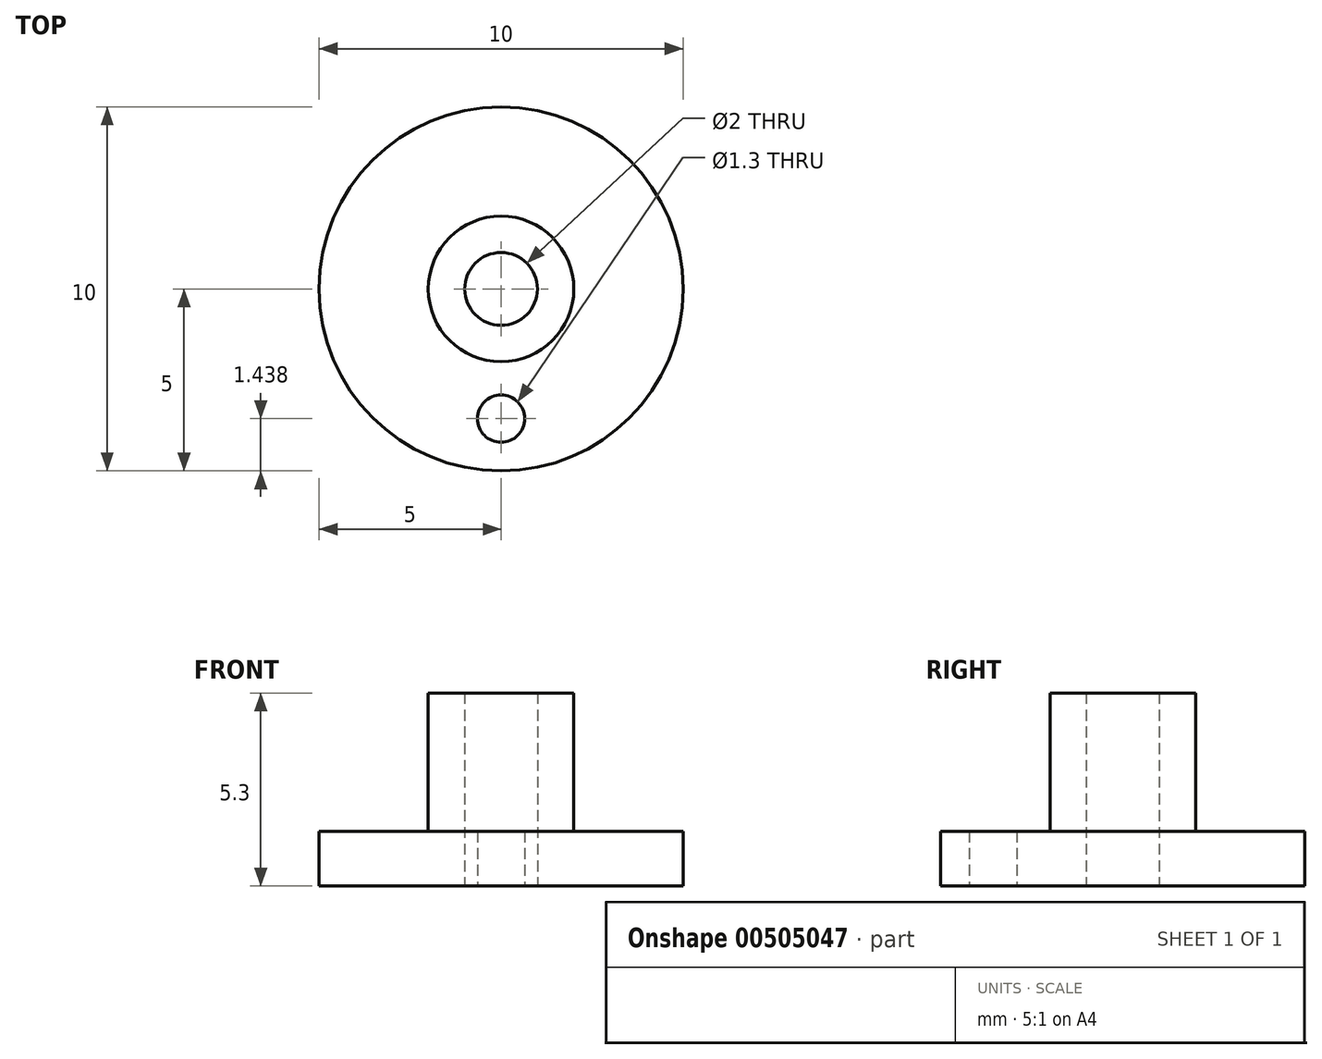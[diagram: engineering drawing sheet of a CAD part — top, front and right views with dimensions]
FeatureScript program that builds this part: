
annotation { "Feature Type Name" : "Feature", "Feature Type Description" : "" }
export const myFeature = defineFeature(function(context is Context, id is Id, definition is map)
    precondition{}
    {
        {
            var Q0;
            Q0=qCreatedBy(makeId("Top.planeOp"),FACE);
            var sketch = newSketch(context, id + "F0", { "sketchPlane" : qUnion([Q0])});
            skCircle(sketch, "E0", {"center": v(0, 0) * mm, "radius": 5 * mm});
            skCircle(sketch, "E1", {"center": v(0, 0) * mm, "radius": 1 * mm});
            skSolve(sketch);
        }
        {
            var Q0;
            Q0=makeQuery(id+"F0.imprint","IMPRINT",FACE,{"disambiguationData":[TD([[makeQuery(id+"F0.imprint","IMPRINT",EDGE,{"derivedFrom":sQuery(id+"F0.wireOp",EDGE,"E1")}),-1.0]])]});
            var Q1;
            {var subQ0=sQuery(id+"F0.wireOp",EDGE,"EI4zZE9N-whVI-OPHs-3LS9-Eucb53RtoGpZ");var subQ1=sQuery(id+"F0.wireOp",EDGE,"E0");var subQ2=makeQuery(id+"F0.imprint","INTERSECT",VERTEX,{"derivedFrom":[subQ1,subQ0]});Q1=makeQuery(id+"F0.imprint","IMPRINT",FACE,{"disambiguationData":[TD([[makeQuery(id+"F0.imprint","IMPRINT",EDGE,{"disambiguationData":[TD([[subQ2,1.0]])],"derivedFrom":subQ1}),-1.0]])]});}
            var Q2;
            {var subQ0=sQuery(id+"F0.wireOp",EDGE,"6d7b41f3-6400-49b5-a72e-f197a9a28993.24.0");var subQ1=sQuery(id+"F0.wireOp",EDGE,"E0");var subQ2=makeQuery(id+"F0.imprint","INTERSECT",VERTEX,{"derivedFrom":[subQ1,subQ0]});Q2=makeQuery(id+"F0.imprint","IMPRINT",FACE,{"disambiguationData":[TD([[makeQuery(id+"F0.imprint","IMPRINT",EDGE,{"disambiguationData":[TD([[subQ2,1.0]])],"derivedFrom":subQ1}),-1.0]])]});}
            var Q3;
            {var subQ0=sQuery(id+"F0.wireOp",EDGE,"6d7b41f3-6400-49b5-a72e-f197a9a28993.25.0");var subQ1=sQuery(id+"F0.wireOp",EDGE,"E0");var subQ2=makeQuery(id+"F0.imprint","INTERSECT",VERTEX,{"derivedFrom":[subQ1,subQ0]});Q3=makeQuery(id+"F0.imprint","IMPRINT",FACE,{"disambiguationData":[TD([[makeQuery(id+"F0.imprint","IMPRINT",EDGE,{"disambiguationData":[TD([[subQ2,1.0]])],"derivedFrom":subQ1}),-1.0]])]});}
            var Q4;
            {var subQ0=sQuery(id+"F0.wireOp",EDGE,"6d7b41f3-6400-49b5-a72e-f197a9a28993.26.0");var subQ1=sQuery(id+"F0.wireOp",EDGE,"E0");var subQ2=makeQuery(id+"F0.imprint","INTERSECT",VERTEX,{"derivedFrom":[subQ1,subQ0]});Q4=makeQuery(id+"F0.imprint","IMPRINT",FACE,{"disambiguationData":[TD([[makeQuery(id+"F0.imprint","IMPRINT",EDGE,{"disambiguationData":[TD([[subQ2,1.0]])],"derivedFrom":subQ1}),-1.0]])]});}
            var Q5;
            {var subQ0=sQuery(id+"F0.wireOp",EDGE,"6d7b41f3-6400-49b5-a72e-f197a9a28993.27.0");var subQ1=sQuery(id+"F0.wireOp",EDGE,"E0");var subQ2=makeQuery(id+"F0.imprint","INTERSECT",VERTEX,{"derivedFrom":[subQ1,subQ0]});Q5=makeQuery(id+"F0.imprint","IMPRINT",FACE,{"disambiguationData":[TD([[makeQuery(id+"F0.imprint","IMPRINT",EDGE,{"disambiguationData":[TD([[subQ2,1.0]])],"derivedFrom":subQ1}),-1.0]])]});}
            var Q6;
            {var subQ0=sQuery(id+"F0.wireOp",EDGE,"6d7b41f3-6400-49b5-a72e-f197a9a28993.28.0");var subQ1=sQuery(id+"F0.wireOp",EDGE,"E0");var subQ2=makeQuery(id+"F0.imprint","INTERSECT",VERTEX,{"derivedFrom":[subQ1,subQ0]});Q6=makeQuery(id+"F0.imprint","IMPRINT",FACE,{"disambiguationData":[TD([[makeQuery(id+"F0.imprint","IMPRINT",EDGE,{"disambiguationData":[TD([[subQ2,1.0]])],"derivedFrom":subQ1}),-1.0]])]});}
            var Q7;
            {var subQ0=sQuery(id+"F0.wireOp",EDGE,"6d7b41f3-6400-49b5-a72e-f197a9a28993.29.0");var subQ1=sQuery(id+"F0.wireOp",EDGE,"E0");var subQ2=makeQuery(id+"F0.imprint","INTERSECT",VERTEX,{"derivedFrom":[subQ1,subQ0]});Q7=makeQuery(id+"F0.imprint","IMPRINT",FACE,{"disambiguationData":[TD([[makeQuery(id+"F0.imprint","IMPRINT",EDGE,{"disambiguationData":[TD([[subQ2,1.0]])],"derivedFrom":subQ1}),-1.0]])]});}
            var Q8;
            {var subQ0=sQuery(id+"F0.wireOp",EDGE,"6d7b41f3-6400-49b5-a72e-f197a9a28993.30.0");var subQ1=sQuery(id+"F0.wireOp",EDGE,"E0");var subQ2=makeQuery(id+"F0.imprint","INTERSECT",VERTEX,{"derivedFrom":[subQ1,subQ0]});Q8=makeQuery(id+"F0.imprint","IMPRINT",FACE,{"disambiguationData":[TD([[makeQuery(id+"F0.imprint","IMPRINT",EDGE,{"disambiguationData":[TD([[subQ2,1.0]])],"derivedFrom":subQ1}),-1.0]])]});}
            var Q9;
            {var subQ0=sQuery(id+"F0.wireOp",EDGE,"rxgSa6x3-vu4U-r9f0-bHfC-lMe1TVJ3Zobz");var subQ1=sQuery(id+"F0.wireOp",EDGE,"E0");var subQ2=makeQuery(id+"F0.imprint","INTERSECT",VERTEX,{"derivedFrom":[subQ1,subQ0]});Q9=makeQuery(id+"F0.imprint","IMPRINT",FACE,{"disambiguationData":[TD([[makeQuery(id+"F0.imprint","IMPRINT",EDGE,{"disambiguationData":[TD([[subQ2,-1.0]])],"derivedFrom":subQ1}),-1.0]])]});}
            var Q10;
            {var subQ0=sQuery(id+"F0.wireOp",EDGE,"6d7b41f3-6400-49b5-a72e-f197a9a28993.1.0");var subQ1=sQuery(id+"F0.wireOp",EDGE,"E0");var subQ2=makeQuery(id+"F0.imprint","INTERSECT",VERTEX,{"derivedFrom":[subQ1,subQ0]});Q10=makeQuery(id+"F0.imprint","IMPRINT",FACE,{"disambiguationData":[TD([[makeQuery(id+"F0.imprint","IMPRINT",EDGE,{"disambiguationData":[TD([[subQ2,1.0]])],"derivedFrom":subQ1}),-1.0]])]});}
            var Q11;
            {var subQ0=sQuery(id+"F0.wireOp",EDGE,"6d7b41f3-6400-49b5-a72e-f197a9a28993.2.0");var subQ1=sQuery(id+"F0.wireOp",EDGE,"E0");var subQ2=makeQuery(id+"F0.imprint","INTERSECT",VERTEX,{"derivedFrom":[subQ1,subQ0]});Q11=makeQuery(id+"F0.imprint","IMPRINT",FACE,{"disambiguationData":[TD([[makeQuery(id+"F0.imprint","IMPRINT",EDGE,{"disambiguationData":[TD([[subQ2,1.0]])],"derivedFrom":subQ1}),-1.0]])]});}
            var Q12;
            {var subQ0=sQuery(id+"F0.wireOp",EDGE,"6d7b41f3-6400-49b5-a72e-f197a9a28993.3.0");var subQ1=sQuery(id+"F0.wireOp",EDGE,"E0");var subQ2=makeQuery(id+"F0.imprint","INTERSECT",VERTEX,{"derivedFrom":[subQ1,subQ0]});Q12=makeQuery(id+"F0.imprint","IMPRINT",FACE,{"disambiguationData":[TD([[makeQuery(id+"F0.imprint","IMPRINT",EDGE,{"disambiguationData":[TD([[subQ2,1.0]])],"derivedFrom":subQ1}),-1.0]])]});}
            var Q13;
            {var subQ0=sQuery(id+"F0.wireOp",EDGE,"6d7b41f3-6400-49b5-a72e-f197a9a28993.4.0");var subQ1=sQuery(id+"F0.wireOp",EDGE,"E0");var subQ2=makeQuery(id+"F0.imprint","INTERSECT",VERTEX,{"derivedFrom":[subQ1,subQ0]});Q13=makeQuery(id+"F0.imprint","IMPRINT",FACE,{"disambiguationData":[TD([[makeQuery(id+"F0.imprint","IMPRINT",EDGE,{"disambiguationData":[TD([[subQ2,1.0]])],"derivedFrom":subQ1}),-1.0]])]});}
            var Q14;
            {var subQ0=sQuery(id+"F0.wireOp",EDGE,"6d7b41f3-6400-49b5-a72e-f197a9a28993.5.0");var subQ1=sQuery(id+"F0.wireOp",EDGE,"E0");var subQ2=makeQuery(id+"F0.imprint","INTERSECT",VERTEX,{"derivedFrom":[subQ1,subQ0]});Q14=makeQuery(id+"F0.imprint","IMPRINT",FACE,{"disambiguationData":[TD([[makeQuery(id+"F0.imprint","IMPRINT",EDGE,{"disambiguationData":[TD([[subQ2,1.0]])],"derivedFrom":subQ1}),-1.0]])]});}
            var Q15;
            {var subQ0=sQuery(id+"F0.wireOp",EDGE,"6d7b41f3-6400-49b5-a72e-f197a9a28993.6.0");var subQ1=sQuery(id+"F0.wireOp",EDGE,"E0");var subQ2=makeQuery(id+"F0.imprint","INTERSECT",VERTEX,{"derivedFrom":[subQ1,subQ0]});Q15=makeQuery(id+"F0.imprint","IMPRINT",FACE,{"disambiguationData":[TD([[makeQuery(id+"F0.imprint","IMPRINT",EDGE,{"disambiguationData":[TD([[subQ2,1.0]])],"derivedFrom":subQ1}),-1.0]])]});}
            var Q16;
            {var subQ0=sQuery(id+"F0.wireOp",EDGE,"6d7b41f3-6400-49b5-a72e-f197a9a28993.7.0");var subQ1=sQuery(id+"F0.wireOp",EDGE,"E0");var subQ2=makeQuery(id+"F0.imprint","INTERSECT",VERTEX,{"derivedFrom":[subQ1,subQ0]});Q16=makeQuery(id+"F0.imprint","IMPRINT",FACE,{"disambiguationData":[TD([[makeQuery(id+"F0.imprint","IMPRINT",EDGE,{"disambiguationData":[TD([[subQ2,1.0]])],"derivedFrom":subQ1}),-1.0]])]});}
            var Q17;
            {var subQ0=sQuery(id+"F0.wireOp",EDGE,"6d7b41f3-6400-49b5-a72e-f197a9a28993.8.0");var subQ1=sQuery(id+"F0.wireOp",EDGE,"E0");var subQ2=makeQuery(id+"F0.imprint","INTERSECT",VERTEX,{"derivedFrom":[subQ1,subQ0]});Q17=makeQuery(id+"F0.imprint","IMPRINT",FACE,{"disambiguationData":[TD([[makeQuery(id+"F0.imprint","IMPRINT",EDGE,{"disambiguationData":[TD([[subQ2,1.0]])],"derivedFrom":subQ1}),-1.0]])]});}
            var Q18;
            {var subQ0=sQuery(id+"F0.wireOp",EDGE,"6d7b41f3-6400-49b5-a72e-f197a9a28993.9.0");var subQ1=sQuery(id+"F0.wireOp",EDGE,"E0");var subQ2=makeQuery(id+"F0.imprint","INTERSECT",VERTEX,{"derivedFrom":[subQ1,subQ0]});Q18=makeQuery(id+"F0.imprint","IMPRINT",FACE,{"disambiguationData":[TD([[makeQuery(id+"F0.imprint","IMPRINT",EDGE,{"disambiguationData":[TD([[subQ2,1.0]])],"derivedFrom":subQ1}),-1.0]])]});}
            var Q19;
            {var subQ0=sQuery(id+"F0.wireOp",EDGE,"6d7b41f3-6400-49b5-a72e-f197a9a28993.10.0");var subQ1=sQuery(id+"F0.wireOp",EDGE,"E0");var subQ2=makeQuery(id+"F0.imprint","INTERSECT",VERTEX,{"derivedFrom":[subQ1,subQ0]});Q19=makeQuery(id+"F0.imprint","IMPRINT",FACE,{"disambiguationData":[TD([[makeQuery(id+"F0.imprint","IMPRINT",EDGE,{"disambiguationData":[TD([[subQ2,1.0]])],"derivedFrom":subQ1}),-1.0]])]});}
            var Q20;
            {var subQ0=sQuery(id+"F0.wireOp",EDGE,"6d7b41f3-6400-49b5-a72e-f197a9a28993.11.0");var subQ1=sQuery(id+"F0.wireOp",EDGE,"E0");var subQ2=makeQuery(id+"F0.imprint","INTERSECT",VERTEX,{"derivedFrom":[subQ1,subQ0]});Q20=makeQuery(id+"F0.imprint","IMPRINT",FACE,{"disambiguationData":[TD([[makeQuery(id+"F0.imprint","IMPRINT",EDGE,{"disambiguationData":[TD([[subQ2,1.0]])],"derivedFrom":subQ1}),-1.0]])]});}
            var Q21;
            {var subQ0=sQuery(id+"F0.wireOp",EDGE,"6d7b41f3-6400-49b5-a72e-f197a9a28993.12.0");var subQ1=sQuery(id+"F0.wireOp",EDGE,"E0");var subQ2=makeQuery(id+"F0.imprint","INTERSECT",VERTEX,{"derivedFrom":[subQ1,subQ0]});Q21=makeQuery(id+"F0.imprint","IMPRINT",FACE,{"disambiguationData":[TD([[makeQuery(id+"F0.imprint","IMPRINT",EDGE,{"disambiguationData":[TD([[subQ2,1.0]])],"derivedFrom":subQ1}),-1.0]])]});}
            var Q22;
            {var subQ0=sQuery(id+"F0.wireOp",EDGE,"6d7b41f3-6400-49b5-a72e-f197a9a28993.13.0");var subQ1=sQuery(id+"F0.wireOp",EDGE,"E0");var subQ2=makeQuery(id+"F0.imprint","INTERSECT",VERTEX,{"derivedFrom":[subQ1,subQ0]});Q22=makeQuery(id+"F0.imprint","IMPRINT",FACE,{"disambiguationData":[TD([[makeQuery(id+"F0.imprint","IMPRINT",EDGE,{"disambiguationData":[TD([[subQ2,1.0]])],"derivedFrom":subQ1}),-1.0]])]});}
            var Q23;
            {var subQ0=sQuery(id+"F0.wireOp",EDGE,"6d7b41f3-6400-49b5-a72e-f197a9a28993.14.0");var subQ1=sQuery(id+"F0.wireOp",EDGE,"E0");var subQ2=makeQuery(id+"F0.imprint","INTERSECT",VERTEX,{"derivedFrom":[subQ1,subQ0]});Q23=makeQuery(id+"F0.imprint","IMPRINT",FACE,{"disambiguationData":[TD([[makeQuery(id+"F0.imprint","IMPRINT",EDGE,{"disambiguationData":[TD([[subQ2,1.0]])],"derivedFrom":subQ1}),-1.0]])]});}
            var Q24;
            {var subQ0=sQuery(id+"F0.wireOp",EDGE,"6d7b41f3-6400-49b5-a72e-f197a9a28993.15.0");var subQ1=sQuery(id+"F0.wireOp",EDGE,"E0");var subQ2=makeQuery(id+"F0.imprint","INTERSECT",VERTEX,{"derivedFrom":[subQ1,subQ0]});Q24=makeQuery(id+"F0.imprint","IMPRINT",FACE,{"disambiguationData":[TD([[makeQuery(id+"F0.imprint","IMPRINT",EDGE,{"disambiguationData":[TD([[subQ2,1.0]])],"derivedFrom":subQ1}),-1.0]])]});}
            var Q25;
            {var subQ0=sQuery(id+"F0.wireOp",EDGE,"6d7b41f3-6400-49b5-a72e-f197a9a28993.16.0");var subQ1=sQuery(id+"F0.wireOp",EDGE,"E0");var subQ2=makeQuery(id+"F0.imprint","INTERSECT",VERTEX,{"derivedFrom":[subQ1,subQ0]});Q25=makeQuery(id+"F0.imprint","IMPRINT",FACE,{"disambiguationData":[TD([[makeQuery(id+"F0.imprint","IMPRINT",EDGE,{"disambiguationData":[TD([[subQ2,1.0]])],"derivedFrom":subQ1}),-1.0]])]});}
            var Q26;
            {var subQ0=sQuery(id+"F0.wireOp",EDGE,"6d7b41f3-6400-49b5-a72e-f197a9a28993.17.0");var subQ1=sQuery(id+"F0.wireOp",EDGE,"E0");var subQ2=makeQuery(id+"F0.imprint","INTERSECT",VERTEX,{"derivedFrom":[subQ1,subQ0]});Q26=makeQuery(id+"F0.imprint","IMPRINT",FACE,{"disambiguationData":[TD([[makeQuery(id+"F0.imprint","IMPRINT",EDGE,{"disambiguationData":[TD([[subQ2,1.0]])],"derivedFrom":subQ1}),-1.0]])]});}
            var Q27;
            {var subQ0=sQuery(id+"F0.wireOp",EDGE,"6d7b41f3-6400-49b5-a72e-f197a9a28993.18.0");var subQ1=sQuery(id+"F0.wireOp",EDGE,"E0");var subQ2=makeQuery(id+"F0.imprint","INTERSECT",VERTEX,{"derivedFrom":[subQ1,subQ0]});Q27=makeQuery(id+"F0.imprint","IMPRINT",FACE,{"disambiguationData":[TD([[makeQuery(id+"F0.imprint","IMPRINT",EDGE,{"disambiguationData":[TD([[subQ2,1.0]])],"derivedFrom":subQ1}),-1.0]])]});}
            var Q28;
            {var subQ0=sQuery(id+"F0.wireOp",EDGE,"6d7b41f3-6400-49b5-a72e-f197a9a28993.19.0");var subQ1=sQuery(id+"F0.wireOp",EDGE,"E0");var subQ2=makeQuery(id+"F0.imprint","INTERSECT",VERTEX,{"derivedFrom":[subQ1,subQ0]});Q28=makeQuery(id+"F0.imprint","IMPRINT",FACE,{"disambiguationData":[TD([[makeQuery(id+"F0.imprint","IMPRINT",EDGE,{"disambiguationData":[TD([[subQ2,1.0]])],"derivedFrom":subQ1}),-1.0]])]});}
            var Q29;
            {var subQ0=sQuery(id+"F0.wireOp",EDGE,"6d7b41f3-6400-49b5-a72e-f197a9a28993.20.0");var subQ1=sQuery(id+"F0.wireOp",EDGE,"E0");var subQ2=makeQuery(id+"F0.imprint","INTERSECT",VERTEX,{"derivedFrom":[subQ1,subQ0]});Q29=makeQuery(id+"F0.imprint","IMPRINT",FACE,{"disambiguationData":[TD([[makeQuery(id+"F0.imprint","IMPRINT",EDGE,{"disambiguationData":[TD([[subQ2,1.0]])],"derivedFrom":subQ1}),-1.0]])]});}
            var Q30;
            {var subQ0=sQuery(id+"F0.wireOp",EDGE,"6d7b41f3-6400-49b5-a72e-f197a9a28993.21.0");var subQ1=sQuery(id+"F0.wireOp",EDGE,"E0");var subQ2=makeQuery(id+"F0.imprint","INTERSECT",VERTEX,{"derivedFrom":[subQ1,subQ0]});Q30=makeQuery(id+"F0.imprint","IMPRINT",FACE,{"disambiguationData":[TD([[makeQuery(id+"F0.imprint","IMPRINT",EDGE,{"disambiguationData":[TD([[subQ2,1.0]])],"derivedFrom":subQ1}),-1.0]])]});}
            var Q31;
            {var subQ0=sQuery(id+"F0.wireOp",EDGE,"6d7b41f3-6400-49b5-a72e-f197a9a28993.22.0");var subQ1=sQuery(id+"F0.wireOp",EDGE,"E0");var subQ2=makeQuery(id+"F0.imprint","INTERSECT",VERTEX,{"derivedFrom":[subQ1,subQ0]});Q31=makeQuery(id+"F0.imprint","IMPRINT",FACE,{"disambiguationData":[TD([[makeQuery(id+"F0.imprint","IMPRINT",EDGE,{"disambiguationData":[TD([[subQ2,1.0]])],"derivedFrom":subQ1}),-1.0]])]});}
            var Q32;
            {var subQ0=sQuery(id+"F0.wireOp",EDGE,"6d7b41f3-6400-49b5-a72e-f197a9a28993.23.0");var subQ1=sQuery(id+"F0.wireOp",EDGE,"E0");var subQ2=makeQuery(id+"F0.imprint","INTERSECT",VERTEX,{"derivedFrom":[subQ1,subQ0]});Q32=makeQuery(id+"F0.imprint","IMPRINT",FACE,{"disambiguationData":[TD([[makeQuery(id+"F0.imprint","IMPRINT",EDGE,{"disambiguationData":[TD([[subQ2,1.0]])],"derivedFrom":subQ1}),-1.0]])]});}
            var Q33;
            {var subQ3=sQuery(id+"F0.wireOp",EDGE,"rxgSa6x3-vu4U-r9f0-bHfC-lMe1TVJ3Zobz");var subQ6=sQuery(id+"F0.wireOp",EDGE,"E0");var subQ9=makeQuery(id+"F0.imprint","INTERSECT",VERTEX,{"derivedFrom":[subQ6,subQ3]});Q33=makeQuery(id+"F0.imprint","IMPRINT",FACE,{"disambiguationData":[TD([[makeQuery(id+"F0.imprint","IMPRINT",EDGE,{"disambiguationData":[TD([[subQ9,1.0]])],"derivedFrom":subQ6}),-1.0]])]});}
            var Q34;
            {var subQ3=sQuery(id+"F0.wireOp",EDGE,"EI4zZE9N-whVI-OPHs-3LS9-Eucb53RtoGpZ");var subQ7=sQuery(id+"F0.wireOp",EDGE,"E0");var subQ8=makeQuery(id+"F0.imprint","INTERSECT",VERTEX,{"derivedFrom":[subQ7,subQ3]});Q34=makeQuery(id+"F0.imprint","IMPRINT",FACE,{"disambiguationData":[TD([[makeQuery(id+"F0.imprint","IMPRINT",EDGE,{"disambiguationData":[TD([[subQ8,-1.0]])],"derivedFrom":subQ7}),-1.0]])]});}
            var Q35;
            {var subQ3=sQuery(id+"F0.wireOp",EDGE,"6d7b41f3-6400-49b5-a72e-f197a9a28993.6.0");var subQ5=sQuery(id+"F0.wireOp",EDGE,"E0");var subQ6=makeQuery(id+"F0.imprint","INTERSECT",VERTEX,{"derivedFrom":[subQ5,subQ3]});Q35=makeQuery(id+"F0.imprint","IMPRINT",FACE,{"disambiguationData":[TD([[makeQuery(id+"F0.imprint","IMPRINT",EDGE,{"disambiguationData":[TD([[subQ6,-1.0]])],"derivedFrom":subQ5}),-1.0]])]});}
            var Q36;
            {var subQ3=sQuery(id+"F0.wireOp",EDGE,"6d7b41f3-6400-49b5-a72e-f197a9a28993.24.0");var subQ7=sQuery(id+"F0.wireOp",EDGE,"E0");var subQ8=makeQuery(id+"F0.imprint","INTERSECT",VERTEX,{"derivedFrom":[subQ7,subQ3]});Q36=makeQuery(id+"F0.imprint","IMPRINT",FACE,{"disambiguationData":[TD([[makeQuery(id+"F0.imprint","IMPRINT",EDGE,{"disambiguationData":[TD([[subQ8,-1.0]])],"derivedFrom":subQ7}),-1.0]])]});}
            var Q37;
            {var subQ3=sQuery(id+"F0.wireOp",EDGE,"6d7b41f3-6400-49b5-a72e-f197a9a28993.14.0");var subQ7=sQuery(id+"F0.wireOp",EDGE,"E0");var subQ8=makeQuery(id+"F0.imprint","INTERSECT",VERTEX,{"derivedFrom":[subQ7,subQ3]});Q37=makeQuery(id+"F0.imprint","IMPRINT",FACE,{"disambiguationData":[TD([[makeQuery(id+"F0.imprint","IMPRINT",EDGE,{"disambiguationData":[TD([[subQ8,-1.0]])],"derivedFrom":subQ7}),-1.0]])]});}
            var Q38;
            {var subQ5=sQuery(id+"F0.wireOp",EDGE,"6d7b41f3-6400-49b5-a72e-f197a9a28993.26.0");var subQ6=sQuery(id+"F0.wireOp",EDGE,"E0");var subQ7=makeQuery(id+"F0.imprint","INTERSECT",VERTEX,{"derivedFrom":[subQ6,subQ5]});Q38=makeQuery(id+"F0.imprint","IMPRINT",FACE,{"disambiguationData":[TD([[makeQuery(id+"F0.imprint","IMPRINT",EDGE,{"disambiguationData":[TD([[subQ7,-1.0]])],"derivedFrom":subQ6}),-1.0]])]});}
            var Q39;
            {var subQ3=sQuery(id+"F0.wireOp",EDGE,"6d7b41f3-6400-49b5-a72e-f197a9a28993.9.0");var subQ7=sQuery(id+"F0.wireOp",EDGE,"E0");var subQ8=makeQuery(id+"F0.imprint","INTERSECT",VERTEX,{"derivedFrom":[subQ7,subQ3]});Q39=makeQuery(id+"F0.imprint","IMPRINT",FACE,{"disambiguationData":[TD([[makeQuery(id+"F0.imprint","IMPRINT",EDGE,{"disambiguationData":[TD([[subQ8,-1.0]])],"derivedFrom":subQ7}),-1.0]])]});}
            var Q40;
            {var subQ3=sQuery(id+"F0.wireOp",EDGE,"6d7b41f3-6400-49b5-a72e-f197a9a28993.7.0");var subQ7=sQuery(id+"F0.wireOp",EDGE,"E0");var subQ8=makeQuery(id+"F0.imprint","INTERSECT",VERTEX,{"derivedFrom":[subQ7,subQ3]});Q40=makeQuery(id+"F0.imprint","IMPRINT",FACE,{"disambiguationData":[TD([[makeQuery(id+"F0.imprint","IMPRINT",EDGE,{"disambiguationData":[TD([[subQ8,-1.0]])],"derivedFrom":subQ7}),-1.0]])]});}
            var Q41;
            {var subQ3=sQuery(id+"F0.wireOp",EDGE,"6d7b41f3-6400-49b5-a72e-f197a9a28993.22.0");var subQ7=sQuery(id+"F0.wireOp",EDGE,"E0");var subQ8=makeQuery(id+"F0.imprint","INTERSECT",VERTEX,{"derivedFrom":[subQ7,subQ3]});Q41=makeQuery(id+"F0.imprint","IMPRINT",FACE,{"disambiguationData":[TD([[makeQuery(id+"F0.imprint","IMPRINT",EDGE,{"disambiguationData":[TD([[subQ8,-1.0]])],"derivedFrom":subQ7}),-1.0]])]});}
            var Q42;
            {var subQ5=sQuery(id+"F0.wireOp",EDGE,"6d7b41f3-6400-49b5-a72e-f197a9a28993.23.0");var subQ6=sQuery(id+"F0.wireOp",EDGE,"E0");var subQ7=makeQuery(id+"F0.imprint","INTERSECT",VERTEX,{"derivedFrom":[subQ6,subQ5]});Q42=makeQuery(id+"F0.imprint","IMPRINT",FACE,{"disambiguationData":[TD([[makeQuery(id+"F0.imprint","IMPRINT",EDGE,{"disambiguationData":[TD([[subQ7,-1.0]])],"derivedFrom":subQ6}),-1.0]])]});}
            var Q43;
            {var subQ3=sQuery(id+"F0.wireOp",EDGE,"6d7b41f3-6400-49b5-a72e-f197a9a28993.4.0");var subQ7=sQuery(id+"F0.wireOp",EDGE,"E0");var subQ8=makeQuery(id+"F0.imprint","INTERSECT",VERTEX,{"derivedFrom":[subQ7,subQ3]});Q43=makeQuery(id+"F0.imprint","IMPRINT",FACE,{"disambiguationData":[TD([[makeQuery(id+"F0.imprint","IMPRINT",EDGE,{"disambiguationData":[TD([[subQ8,-1.0]])],"derivedFrom":subQ7}),-1.0]])]});}
            var Q44;
            {var subQ0=sQuery(id+"F0.wireOp",EDGE,"6d7b41f3-6400-49b5-a72e-f197a9a28993.1.1");var subQ1=sQuery(id+"F0.wireOp",EDGE,"E0");var subQ2=makeQuery(id+"F0.imprint","INTERSECT",VERTEX,{"derivedFrom":[subQ1,subQ0]});Q44=makeQuery(id+"F0.imprint","IMPRINT",FACE,{"disambiguationData":[TD([[makeQuery(id+"F0.imprint","IMPRINT",EDGE,{"disambiguationData":[TD([[subQ2,1.0]])],"derivedFrom":subQ1}),-1.0]])]});}
            var Q45;
            {var subQ3=sQuery(id+"F0.wireOp",EDGE,"6d7b41f3-6400-49b5-a72e-f197a9a28993.10.0");var subQ7=sQuery(id+"F0.wireOp",EDGE,"E0");var subQ8=makeQuery(id+"F0.imprint","INTERSECT",VERTEX,{"derivedFrom":[subQ7,subQ3]});Q45=makeQuery(id+"F0.imprint","IMPRINT",FACE,{"disambiguationData":[TD([[makeQuery(id+"F0.imprint","IMPRINT",EDGE,{"disambiguationData":[TD([[subQ8,-1.0]])],"derivedFrom":subQ7}),-1.0]])]});}
            var Q46;
            {var subQ3=sQuery(id+"F0.wireOp",EDGE,"6d7b41f3-6400-49b5-a72e-f197a9a28993.21.0");var subQ7=sQuery(id+"F0.wireOp",EDGE,"E0");var subQ8=makeQuery(id+"F0.imprint","INTERSECT",VERTEX,{"derivedFrom":[subQ7,subQ3]});Q46=makeQuery(id+"F0.imprint","IMPRINT",FACE,{"disambiguationData":[TD([[makeQuery(id+"F0.imprint","IMPRINT",EDGE,{"disambiguationData":[TD([[subQ8,-1.0]])],"derivedFrom":subQ7}),-1.0]])]});}
            var Q47;
            {var subQ3=sQuery(id+"F0.wireOp",EDGE,"6d7b41f3-6400-49b5-a72e-f197a9a28993.2.0");var subQ7=sQuery(id+"F0.wireOp",EDGE,"E0");var subQ8=makeQuery(id+"F0.imprint","INTERSECT",VERTEX,{"derivedFrom":[subQ7,subQ3]});Q47=makeQuery(id+"F0.imprint","IMPRINT",FACE,{"disambiguationData":[TD([[makeQuery(id+"F0.imprint","IMPRINT",EDGE,{"disambiguationData":[TD([[subQ8,-1.0]])],"derivedFrom":subQ7}),-1.0]])]});}
            var Q48;
            {var subQ3=sQuery(id+"F0.wireOp",EDGE,"6d7b41f3-6400-49b5-a72e-f197a9a28993.27.0");var subQ7=sQuery(id+"F0.wireOp",EDGE,"E0");var subQ8=makeQuery(id+"F0.imprint","INTERSECT",VERTEX,{"derivedFrom":[subQ7,subQ3]});Q48=makeQuery(id+"F0.imprint","IMPRINT",FACE,{"disambiguationData":[TD([[makeQuery(id+"F0.imprint","IMPRINT",EDGE,{"disambiguationData":[TD([[subQ8,-1.0]])],"derivedFrom":subQ7}),-1.0]])]});}
            var Q49;
            {var subQ3=sQuery(id+"F0.wireOp",EDGE,"6d7b41f3-6400-49b5-a72e-f197a9a28993.15.0");var subQ7=sQuery(id+"F0.wireOp",EDGE,"E0");var subQ8=makeQuery(id+"F0.imprint","INTERSECT",VERTEX,{"derivedFrom":[subQ7,subQ3]});Q49=makeQuery(id+"F0.imprint","IMPRINT",FACE,{"disambiguationData":[TD([[makeQuery(id+"F0.imprint","IMPRINT",EDGE,{"disambiguationData":[TD([[subQ8,-1.0]])],"derivedFrom":subQ7}),-1.0]])]});}
            var Q50;
            {var subQ3=sQuery(id+"F0.wireOp",EDGE,"6d7b41f3-6400-49b5-a72e-f197a9a28993.16.0");var subQ7=sQuery(id+"F0.wireOp",EDGE,"E0");var subQ8=makeQuery(id+"F0.imprint","INTERSECT",VERTEX,{"derivedFrom":[subQ7,subQ3]});Q50=makeQuery(id+"F0.imprint","IMPRINT",FACE,{"disambiguationData":[TD([[makeQuery(id+"F0.imprint","IMPRINT",EDGE,{"disambiguationData":[TD([[subQ8,-1.0]])],"derivedFrom":subQ7}),-1.0]])]});}
            var Q51;
            {var subQ5=sQuery(id+"F0.wireOp",EDGE,"6d7b41f3-6400-49b5-a72e-f197a9a28993.8.0");var subQ6=sQuery(id+"F0.wireOp",EDGE,"E0");var subQ7=makeQuery(id+"F0.imprint","INTERSECT",VERTEX,{"derivedFrom":[subQ6,subQ5]});Q51=makeQuery(id+"F0.imprint","IMPRINT",FACE,{"disambiguationData":[TD([[makeQuery(id+"F0.imprint","IMPRINT",EDGE,{"disambiguationData":[TD([[subQ7,-1.0]])],"derivedFrom":subQ6}),-1.0]])]});}
            var Q52;
            {var subQ3=sQuery(id+"F0.wireOp",EDGE,"6d7b41f3-6400-49b5-a72e-f197a9a28993.25.0");var subQ7=sQuery(id+"F0.wireOp",EDGE,"E0");var subQ8=makeQuery(id+"F0.imprint","INTERSECT",VERTEX,{"derivedFrom":[subQ7,subQ3]});Q52=makeQuery(id+"F0.imprint","IMPRINT",FACE,{"disambiguationData":[TD([[makeQuery(id+"F0.imprint","IMPRINT",EDGE,{"disambiguationData":[TD([[subQ8,-1.0]])],"derivedFrom":subQ7}),-1.0]])]});}
            var Q53;
            {var subQ5=sQuery(id+"F0.wireOp",EDGE,"6d7b41f3-6400-49b5-a72e-f197a9a28993.18.0");var subQ6=sQuery(id+"F0.wireOp",EDGE,"E0");var subQ7=makeQuery(id+"F0.imprint","INTERSECT",VERTEX,{"derivedFrom":[subQ6,subQ5]});Q53=makeQuery(id+"F0.imprint","IMPRINT",FACE,{"disambiguationData":[TD([[makeQuery(id+"F0.imprint","IMPRINT",EDGE,{"disambiguationData":[TD([[subQ7,-1.0]])],"derivedFrom":subQ6}),-1.0]])]});}
            var Q54;
            {var subQ3=sQuery(id+"F0.wireOp",EDGE,"6d7b41f3-6400-49b5-a72e-f197a9a28993.5.0");var subQ7=sQuery(id+"F0.wireOp",EDGE,"E0");var subQ8=makeQuery(id+"F0.imprint","INTERSECT",VERTEX,{"derivedFrom":[subQ7,subQ3]});Q54=makeQuery(id+"F0.imprint","IMPRINT",FACE,{"disambiguationData":[TD([[makeQuery(id+"F0.imprint","IMPRINT",EDGE,{"disambiguationData":[TD([[subQ8,-1.0]])],"derivedFrom":subQ7}),-1.0]])]});}
            var Q55;
            {var subQ3=sQuery(id+"F0.wireOp",EDGE,"6d7b41f3-6400-49b5-a72e-f197a9a28993.28.0");var subQ7=sQuery(id+"F0.wireOp",EDGE,"E0");var subQ8=makeQuery(id+"F0.imprint","INTERSECT",VERTEX,{"derivedFrom":[subQ7,subQ3]});Q55=makeQuery(id+"F0.imprint","IMPRINT",FACE,{"disambiguationData":[TD([[makeQuery(id+"F0.imprint","IMPRINT",EDGE,{"disambiguationData":[TD([[subQ8,-1.0]])],"derivedFrom":subQ7}),-1.0]])]});}
            var Q56;
            {var subQ3=sQuery(id+"F0.wireOp",EDGE,"6d7b41f3-6400-49b5-a72e-f197a9a28993.11.0");var subQ7=sQuery(id+"F0.wireOp",EDGE,"E0");var subQ8=makeQuery(id+"F0.imprint","INTERSECT",VERTEX,{"derivedFrom":[subQ7,subQ3]});Q56=makeQuery(id+"F0.imprint","IMPRINT",FACE,{"disambiguationData":[TD([[makeQuery(id+"F0.imprint","IMPRINT",EDGE,{"disambiguationData":[TD([[subQ8,-1.0]])],"derivedFrom":subQ7}),-1.0]])]});}
            var Q57;
            {var subQ3=sQuery(id+"F0.wireOp",EDGE,"6d7b41f3-6400-49b5-a72e-f197a9a28993.12.0");var subQ7=sQuery(id+"F0.wireOp",EDGE,"E0");var subQ8=makeQuery(id+"F0.imprint","INTERSECT",VERTEX,{"derivedFrom":[subQ7,subQ3]});Q57=makeQuery(id+"F0.imprint","IMPRINT",FACE,{"disambiguationData":[TD([[makeQuery(id+"F0.imprint","IMPRINT",EDGE,{"disambiguationData":[TD([[subQ8,-1.0]])],"derivedFrom":subQ7}),-1.0]])]});}
            var Q58;
            {var subQ3=sQuery(id+"F0.wireOp",EDGE,"6d7b41f3-6400-49b5-a72e-f197a9a28993.19.0");var subQ7=sQuery(id+"F0.wireOp",EDGE,"E0");var subQ8=makeQuery(id+"F0.imprint","INTERSECT",VERTEX,{"derivedFrom":[subQ7,subQ3]});Q58=makeQuery(id+"F0.imprint","IMPRINT",FACE,{"disambiguationData":[TD([[makeQuery(id+"F0.imprint","IMPRINT",EDGE,{"disambiguationData":[TD([[subQ8,-1.0]])],"derivedFrom":subQ7}),-1.0]])]});}
            var Q59;
            {var subQ5=sQuery(id+"F0.wireOp",EDGE,"6d7b41f3-6400-49b5-a72e-f197a9a28993.13.0");var subQ6=sQuery(id+"F0.wireOp",EDGE,"E0");var subQ7=makeQuery(id+"F0.imprint","INTERSECT",VERTEX,{"derivedFrom":[subQ6,subQ5]});Q59=makeQuery(id+"F0.imprint","IMPRINT",FACE,{"disambiguationData":[TD([[makeQuery(id+"F0.imprint","IMPRINT",EDGE,{"disambiguationData":[TD([[subQ7,-1.0]])],"derivedFrom":subQ6}),-1.0]])]});}
            var Q60;
            {var subQ3=sQuery(id+"F0.wireOp",EDGE,"6d7b41f3-6400-49b5-a72e-f197a9a28993.20.0");var subQ7=sQuery(id+"F0.wireOp",EDGE,"E0");var subQ8=makeQuery(id+"F0.imprint","INTERSECT",VERTEX,{"derivedFrom":[subQ7,subQ3]});Q60=makeQuery(id+"F0.imprint","IMPRINT",FACE,{"disambiguationData":[TD([[makeQuery(id+"F0.imprint","IMPRINT",EDGE,{"disambiguationData":[TD([[subQ8,-1.0]])],"derivedFrom":subQ7}),-1.0]])]});}
            var Q61;
            {var subQ3=sQuery(id+"F0.wireOp",EDGE,"6d7b41f3-6400-49b5-a72e-f197a9a28993.1.0");var subQ7=sQuery(id+"F0.wireOp",EDGE,"E0");var subQ8=makeQuery(id+"F0.imprint","INTERSECT",VERTEX,{"derivedFrom":[subQ7,subQ3]});Q61=makeQuery(id+"F0.imprint","IMPRINT",FACE,{"disambiguationData":[TD([[makeQuery(id+"F0.imprint","IMPRINT",EDGE,{"disambiguationData":[TD([[subQ8,-1.0]])],"derivedFrom":subQ7}),-1.0]])]});}
            var Q62;
            {var subQ5=sQuery(id+"F0.wireOp",EDGE,"6d7b41f3-6400-49b5-a72e-f197a9a28993.3.0");var subQ6=sQuery(id+"F0.wireOp",EDGE,"E0");var subQ7=makeQuery(id+"F0.imprint","INTERSECT",VERTEX,{"derivedFrom":[subQ6,subQ5]});Q62=makeQuery(id+"F0.imprint","IMPRINT",FACE,{"disambiguationData":[TD([[makeQuery(id+"F0.imprint","IMPRINT",EDGE,{"disambiguationData":[TD([[subQ7,-1.0]])],"derivedFrom":subQ6}),-1.0]])]});}
            var Q63;
            {var subQ3=sQuery(id+"F0.wireOp",EDGE,"6d7b41f3-6400-49b5-a72e-f197a9a28993.17.0");var subQ5=sQuery(id+"F0.wireOp",EDGE,"E0");var subQ6=makeQuery(id+"F0.imprint","INTERSECT",VERTEX,{"derivedFrom":[subQ5,subQ3]});Q63=makeQuery(id+"F0.imprint","IMPRINT",FACE,{"disambiguationData":[TD([[makeQuery(id+"F0.imprint","IMPRINT",EDGE,{"disambiguationData":[TD([[subQ6,-1.0]])],"derivedFrom":subQ5}),-1.0]])]});}
            var Q64;
            {var subQ3=sQuery(id+"F0.wireOp",EDGE,"6d7b41f3-6400-49b5-a72e-f197a9a28993.29.0");var subQ5=sQuery(id+"F0.wireOp",EDGE,"E0");var subQ6=makeQuery(id+"F0.imprint","INTERSECT",VERTEX,{"derivedFrom":[subQ5,subQ3]});Q64=makeQuery(id+"F0.imprint","IMPRINT",FACE,{"disambiguationData":[TD([[makeQuery(id+"F0.imprint","IMPRINT",EDGE,{"disambiguationData":[TD([[subQ6,-1.0]])],"derivedFrom":subQ5}),-1.0]])]});}
            extrude(context, id + "F1", {"entities" : qUnion([Q0, Q1, Q2, Q3, Q4, Q5, Q6, Q7, Q8, Q9, Q10, Q11, Q12, Q13, Q14, Q15, Q16, Q17, Q18, Q19, Q20, Q21, Q22, Q23, Q24, Q25, Q26, Q27, Q28, Q29, Q30, Q31, Q32, Q33, Q34, Q35, Q36, Q37, Q38, Q39, Q40, Q41, Q42, Q43, Q44, Q45, Q46, Q47, Q48, Q49, Q50, Q51, Q52, Q53, Q54, Q55, Q56, Q57, Q58, Q59, Q60, Q61, Q62, Q63, Q64]), "depth" : 1.5 * mm});
        }
        {
            var Q0;
            Q0=makeQuery(id+"F1.opExtrude","CAP_FACE",FACE,{"disambiguationData":[OSD([sQuery(id+"F0.wireOp",EDGE,"E0"),sQuery(id+"F0.wireOp",EDGE,"E1"),sQuery(id+"F0.wireOp",EDGE,"EI4zZE9N-whVI-OPHs-3LS9-Eucb53RtoGpZ"),sQuery(id+"F0.wireOp",EDGE,"rxgSa6x3-vu4U-r9f0-bHfC-lMe1TVJ3Zobz"),sQuery(id+"F0.wireOp",EDGE,"2ae64cd4-93b4-47b9-bf13-a57fa4e7248b.1.0"),sQuery(id+"F0.wireOp",EDGE,"2ae64cd4-93b4-47b9-bf13-a57fa4e7248b.1.1"),sQuery(id+"F0.wireOp",EDGE,"2ae64cd4-93b4-47b9-bf13-a57fa4e7248b.2.0"),sQuery(id+"F0.wireOp",EDGE,"2ae64cd4-93b4-47b9-bf13-a57fa4e7248b.2.1"),sQuery(id+"F0.wireOp",EDGE,"2ae64cd4-93b4-47b9-bf13-a57fa4e7248b.3.0"),sQuery(id+"F0.wireOp",EDGE,"2ae64cd4-93b4-47b9-bf13-a57fa4e7248b.3.1"),sQuery(id+"F0.wireOp",EDGE,"2ae64cd4-93b4-47b9-bf13-a57fa4e7248b.4.0"),sQuery(id+"F0.wireOp",EDGE,"2ae64cd4-93b4-47b9-bf13-a57fa4e7248b.4.1"),sQuery(id+"F0.wireOp",EDGE,"2ae64cd4-93b4-47b9-bf13-a57fa4e7248b.5.0"),sQuery(id+"F0.wireOp",EDGE,"2ae64cd4-93b4-47b9-bf13-a57fa4e7248b.5.1"),sQuery(id+"F0.wireOp",EDGE,"2ae64cd4-93b4-47b9-bf13-a57fa4e7248b.6.0"),sQuery(id+"F0.wireOp",EDGE,"2ae64cd4-93b4-47b9-bf13-a57fa4e7248b.6.1"),sQuery(id+"F0.wireOp",EDGE,"2ae64cd4-93b4-47b9-bf13-a57fa4e7248b.7.0"),sQuery(id+"F0.wireOp",EDGE,"2ae64cd4-93b4-47b9-bf13-a57fa4e7248b.7.1"),sQuery(id+"F0.wireOp",EDGE,"2ae64cd4-93b4-47b9-bf13-a57fa4e7248b.8.0"),sQuery(id+"F0.wireOp",EDGE,"2ae64cd4-93b4-47b9-bf13-a57fa4e7248b.8.1"),sQuery(id+"F0.wireOp",EDGE,"2ae64cd4-93b4-47b9-bf13-a57fa4e7248b.9.0"),sQuery(id+"F0.wireOp",EDGE,"2ae64cd4-93b4-47b9-bf13-a57fa4e7248b.9.1"),sQuery(id+"F0.wireOp",EDGE,"2ae64cd4-93b4-47b9-bf13-a57fa4e7248b.10.0"),sQuery(id+"F0.wireOp",EDGE,"2ae64cd4-93b4-47b9-bf13-a57fa4e7248b.10.1"),sQuery(id+"F0.wireOp",EDGE,"2ae64cd4-93b4-47b9-bf13-a57fa4e7248b.11.0"),sQuery(id+"F0.wireOp",EDGE,"2ae64cd4-93b4-47b9-bf13-a57fa4e7248b.11.1"),sQuery(id+"F0.wireOp",EDGE,"2ae64cd4-93b4-47b9-bf13-a57fa4e7248b.12.0"),sQuery(id+"F0.wireOp",EDGE,"2ae64cd4-93b4-47b9-bf13-a57fa4e7248b.12.1"),sQuery(id+"F0.wireOp",EDGE,"2ae64cd4-93b4-47b9-bf13-a57fa4e7248b.13.0"),sQuery(id+"F0.wireOp",EDGE,"2ae64cd4-93b4-47b9-bf13-a57fa4e7248b.13.1"),sQuery(id+"F0.wireOp",EDGE,"2ae64cd4-93b4-47b9-bf13-a57fa4e7248b.14.0"),sQuery(id+"F0.wireOp",EDGE,"2ae64cd4-93b4-47b9-bf13-a57fa4e7248b.14.1"),sQuery(id+"F0.wireOp",EDGE,"2ae64cd4-93b4-47b9-bf13-a57fa4e7248b.15.0"),sQuery(id+"F0.wireOp",EDGE,"2ae64cd4-93b4-47b9-bf13-a57fa4e7248b.15.1"),sQuery(id+"F0.wireOp",EDGE,"2ae64cd4-93b4-47b9-bf13-a57fa4e7248b.16.0"),sQuery(id+"F0.wireOp",EDGE,"2ae64cd4-93b4-47b9-bf13-a57fa4e7248b.16.1"),sQuery(id+"F0.wireOp",EDGE,"2ae64cd4-93b4-47b9-bf13-a57fa4e7248b.17.0"),sQuery(id+"F0.wireOp",EDGE,"2ae64cd4-93b4-47b9-bf13-a57fa4e7248b.17.1"),sQuery(id+"F0.wireOp",EDGE,"2ae64cd4-93b4-47b9-bf13-a57fa4e7248b.18.0"),sQuery(id+"F0.wireOp",EDGE,"2ae64cd4-93b4-47b9-bf13-a57fa4e7248b.18.1"),sQuery(id+"F0.wireOp",EDGE,"2ae64cd4-93b4-47b9-bf13-a57fa4e7248b.19.0"),sQuery(id+"F0.wireOp",EDGE,"2ae64cd4-93b4-47b9-bf13-a57fa4e7248b.19.1"),sQuery(id+"F0.wireOp",EDGE,"2ae64cd4-93b4-47b9-bf13-a57fa4e7248b.20.0"),sQuery(id+"F0.wireOp",EDGE,"2ae64cd4-93b4-47b9-bf13-a57fa4e7248b.20.1"),sQuery(id+"F0.wireOp",EDGE,"2ae64cd4-93b4-47b9-bf13-a57fa4e7248b.21.0"),sQuery(id+"F0.wireOp",EDGE,"2ae64cd4-93b4-47b9-bf13-a57fa4e7248b.21.1"),sQuery(id+"F0.wireOp",EDGE,"2ae64cd4-93b4-47b9-bf13-a57fa4e7248b.22.0"),sQuery(id+"F0.wireOp",EDGE,"2ae64cd4-93b4-47b9-bf13-a57fa4e7248b.22.1"),sQuery(id+"F0.wireOp",EDGE,"2ae64cd4-93b4-47b9-bf13-a57fa4e7248b.23.0"),sQuery(id+"F0.wireOp",EDGE,"2ae64cd4-93b4-47b9-bf13-a57fa4e7248b.23.1"),sQuery(id+"F0.wireOp",EDGE,"2ae64cd4-93b4-47b9-bf13-a57fa4e7248b.24.0"),sQuery(id+"F0.wireOp",EDGE,"2ae64cd4-93b4-47b9-bf13-a57fa4e7248b.24.1"),sQuery(id+"F0.wireOp",EDGE,"2ae64cd4-93b4-47b9-bf13-a57fa4e7248b.25.0"),sQuery(id+"F0.wireOp",EDGE,"2ae64cd4-93b4-47b9-bf13-a57fa4e7248b.25.1"),sQuery(id+"F0.wireOp",EDGE,"2ae64cd4-93b4-47b9-bf13-a57fa4e7248b.26.0"),sQuery(id+"F0.wireOp",EDGE,"2ae64cd4-93b4-47b9-bf13-a57fa4e7248b.26.1"),sQuery(id+"F0.wireOp",EDGE,"2ae64cd4-93b4-47b9-bf13-a57fa4e7248b.27.0"),sQuery(id+"F0.wireOp",EDGE,"2ae64cd4-93b4-47b9-bf13-a57fa4e7248b.27.1"),sQuery(id+"F0.wireOp",EDGE,"2ae64cd4-93b4-47b9-bf13-a57fa4e7248b.28.0"),sQuery(id+"F0.wireOp",EDGE,"2ae64cd4-93b4-47b9-bf13-a57fa4e7248b.28.1"),sQuery(id+"F0.wireOp",EDGE,"2ae64cd4-93b4-47b9-bf13-a57fa4e7248b.29.0"),sQuery(id+"F0.wireOp",EDGE,"2ae64cd4-93b4-47b9-bf13-a57fa4e7248b.29.1"),sQuery(id+"F0.wireOp",EDGE,"2ae64cd4-93b4-47b9-bf13-a57fa4e7248b.30.0"),sQuery(id+"F0.wireOp",EDGE,"2ae64cd4-93b4-47b9-bf13-a57fa4e7248b.30.1"),sQuery(id+"F0.wireOp",EDGE,"2ae64cd4-93b4-47b9-bf13-a57fa4e7248b.31.0"),sQuery(id+"F0.wireOp",EDGE,"2ae64cd4-93b4-47b9-bf13-a57fa4e7248b.31.1"),sQuery(id+"F0.wireOp",EDGE,"2ae64cd4-93b4-47b9-bf13-a57fa4e7248b.32.0"),sQuery(id+"F0.wireOp",EDGE,"2ae64cd4-93b4-47b9-bf13-a57fa4e7248b.32.1"),sQuery(id+"F0.wireOp",EDGE,"2ae64cd4-93b4-47b9-bf13-a57fa4e7248b.33.0"),sQuery(id+"F0.wireOp",EDGE,"2ae64cd4-93b4-47b9-bf13-a57fa4e7248b.33.1"),sQuery(id+"F0.wireOp",EDGE,"2ae64cd4-93b4-47b9-bf13-a57fa4e7248b.34.0"),sQuery(id+"F0.wireOp",EDGE,"2ae64cd4-93b4-47b9-bf13-a57fa4e7248b.34.1"),sQuery(id+"F0.wireOp",EDGE,"2ae64cd4-93b4-47b9-bf13-a57fa4e7248b.35.0"),sQuery(id+"F0.wireOp",EDGE,"2ae64cd4-93b4-47b9-bf13-a57fa4e7248b.35.1"),sQuery(id+"F0.wireOp",EDGE,"2ae64cd4-93b4-47b9-bf13-a57fa4e7248b.36.0"),sQuery(id+"F0.wireOp",EDGE,"2ae64cd4-93b4-47b9-bf13-a57fa4e7248b.36.1"),sQuery(id+"F0.wireOp",EDGE,"2ae64cd4-93b4-47b9-bf13-a57fa4e7248b.37.0"),sQuery(id+"F0.wireOp",EDGE,"2ae64cd4-93b4-47b9-bf13-a57fa4e7248b.37.1"),sQuery(id+"F0.wireOp",EDGE,"2ae64cd4-93b4-47b9-bf13-a57fa4e7248b.38.0"),sQuery(id+"F0.wireOp",EDGE,"2ae64cd4-93b4-47b9-bf13-a57fa4e7248b.38.1"),sQuery(id+"F0.wireOp",EDGE,"2ae64cd4-93b4-47b9-bf13-a57fa4e7248b.39.0"),sQuery(id+"F0.wireOp",EDGE,"2ae64cd4-93b4-47b9-bf13-a57fa4e7248b.39.1"),sQuery(id+"F0.wireOp",EDGE,"2ae64cd4-93b4-47b9-bf13-a57fa4e7248b.40.0"),sQuery(id+"F0.wireOp",EDGE,"2ae64cd4-93b4-47b9-bf13-a57fa4e7248b.40.1"),sQuery(id+"F0.wireOp",EDGE,"2ae64cd4-93b4-47b9-bf13-a57fa4e7248b.41.0"),sQuery(id+"F0.wireOp",EDGE,"2ae64cd4-93b4-47b9-bf13-a57fa4e7248b.41.1"),sQuery(id+"F0.wireOp",EDGE,"2ae64cd4-93b4-47b9-bf13-a57fa4e7248b.42.0"),sQuery(id+"F0.wireOp",EDGE,"2ae64cd4-93b4-47b9-bf13-a57fa4e7248b.42.1"),sQuery(id+"F0.wireOp",EDGE,"2ae64cd4-93b4-47b9-bf13-a57fa4e7248b.43.0"),sQuery(id+"F0.wireOp",EDGE,"2ae64cd4-93b4-47b9-bf13-a57fa4e7248b.43.1"),sQuery(id+"F0.wireOp",EDGE,"2ae64cd4-93b4-47b9-bf13-a57fa4e7248b.44.0"),sQuery(id+"F0.wireOp",EDGE,"2ae64cd4-93b4-47b9-bf13-a57fa4e7248b.44.1"),sQuery(id+"F0.wireOp",EDGE,"2ae64cd4-93b4-47b9-bf13-a57fa4e7248b.45.0"),sQuery(id+"F0.wireOp",EDGE,"2ae64cd4-93b4-47b9-bf13-a57fa4e7248b.45.1"),sQuery(id+"F0.wireOp",EDGE,"2ae64cd4-93b4-47b9-bf13-a57fa4e7248b.46.0"),sQuery(id+"F0.wireOp",EDGE,"2ae64cd4-93b4-47b9-bf13-a57fa4e7248b.46.1"),sQuery(id+"F0.wireOp",EDGE,"2ae64cd4-93b4-47b9-bf13-a57fa4e7248b.47.0"),sQuery(id+"F0.wireOp",EDGE,"2ae64cd4-93b4-47b9-bf13-a57fa4e7248b.47.1"),sQuery(id+"F0.wireOp",EDGE,"2ae64cd4-93b4-47b9-bf13-a57fa4e7248b.48.0"),sQuery(id+"F0.wireOp",EDGE,"2ae64cd4-93b4-47b9-bf13-a57fa4e7248b.48.1"),sQuery(id+"F0.wireOp",EDGE,"2ae64cd4-93b4-47b9-bf13-a57fa4e7248b.49.0"),sQuery(id+"F0.wireOp",EDGE,"2ae64cd4-93b4-47b9-bf13-a57fa4e7248b.49.1")])],"isStart":false});
            var sketch = newSketch(context, id + "F2", { "sketchPlane" : qUnion([Q0])});
            skCircle(sketch, "E2", {"center": v(0, 0) * mm, "radius": 2 * mm});
            skCircle(sketch, "E3", {"center": v(0, 0) * mm, "radius": 1 * mm});
            skSolve(sketch);
        }
        {
            var Q0;
            Q0=makeQuery(id+"F2.imprint","IMPRINT",FACE,{"disambiguationData":[TD([[makeQuery(id+"F2.imprint","IMPRINT",EDGE,{"derivedFrom":sQuery(id+"F2.wireOp",EDGE,"E3")}),-1.0]])]});
            var Q1;
            {var subQ0=sQuery(id+"F2.wireOp",EDGE,"ef46eeef-f85e-4314-bc99-e56e5a110b71.1.0");Q1=makeQuery(id+"F2.imprint","IMPRINT",FACE,{"disambiguationData":[TD([[makeQuery(id+"F2.imprint","IMPRINT",EDGE,{"derivedFrom":subQ0}),-1.0]])]});}
            var Q2;
            {var subQ0=sQuery(id+"F2.wireOp",EDGE,"AXtbOmny-Rolw-DFvu-AzKX-92h4mGOaohQE");Q2=makeQuery(id+"F2.imprint","IMPRINT",FACE,{"disambiguationData":[TD([[makeQuery(id+"F2.imprint","IMPRINT",EDGE,{"derivedFrom":subQ0}),-1.0]])]});}
            var Q3;
            {var subQ0=sQuery(id+"F2.wireOp",EDGE,"ef46eeef-f85e-4314-bc99-e56e5a110b71.9.0");Q3=makeQuery(id+"F2.imprint","IMPRINT",FACE,{"disambiguationData":[TD([[makeQuery(id+"F2.imprint","IMPRINT",EDGE,{"derivedFrom":subQ0}),-1.0]])]});}
            var Q4;
            {var subQ0=sQuery(id+"F2.wireOp",EDGE,"ef46eeef-f85e-4314-bc99-e56e5a110b71.8.0");Q4=makeQuery(id+"F2.imprint","IMPRINT",FACE,{"disambiguationData":[TD([[makeQuery(id+"F2.imprint","IMPRINT",EDGE,{"derivedFrom":subQ0}),-1.0]])]});}
            var Q5;
            {var subQ0=sQuery(id+"F2.wireOp",EDGE,"ef46eeef-f85e-4314-bc99-e56e5a110b71.7.0");Q5=makeQuery(id+"F2.imprint","IMPRINT",FACE,{"disambiguationData":[TD([[makeQuery(id+"F2.imprint","IMPRINT",EDGE,{"derivedFrom":subQ0}),-1.0]])]});}
            var Q6;
            {var subQ0=sQuery(id+"F2.wireOp",EDGE,"ef46eeef-f85e-4314-bc99-e56e5a110b71.6.0");Q6=makeQuery(id+"F2.imprint","IMPRINT",FACE,{"disambiguationData":[TD([[makeQuery(id+"F2.imprint","IMPRINT",EDGE,{"derivedFrom":subQ0}),-1.0]])]});}
            var Q7;
            {var subQ0=sQuery(id+"F2.wireOp",EDGE,"ef46eeef-f85e-4314-bc99-e56e5a110b71.5.0");Q7=makeQuery(id+"F2.imprint","IMPRINT",FACE,{"disambiguationData":[TD([[makeQuery(id+"F2.imprint","IMPRINT",EDGE,{"derivedFrom":subQ0}),-1.0]])]});}
            var Q8;
            {var subQ0=sQuery(id+"F2.wireOp",EDGE,"ef46eeef-f85e-4314-bc99-e56e5a110b71.2.0");Q8=makeQuery(id+"F2.imprint","IMPRINT",FACE,{"disambiguationData":[TD([[makeQuery(id+"F2.imprint","IMPRINT",EDGE,{"derivedFrom":subQ0}),-1.0]])]});}
            var Q9;
            {var subQ0=sQuery(id+"F2.wireOp",EDGE,"ef46eeef-f85e-4314-bc99-e56e5a110b71.3.0");Q9=makeQuery(id+"F2.imprint","IMPRINT",FACE,{"disambiguationData":[TD([[makeQuery(id+"F2.imprint","IMPRINT",EDGE,{"derivedFrom":subQ0}),-1.0]])]});}
            var Q10;
            {var subQ0=sQuery(id+"F2.wireOp",EDGE,"ef46eeef-f85e-4314-bc99-e56e5a110b71.4.0");Q10=makeQuery(id+"F2.imprint","IMPRINT",FACE,{"disambiguationData":[TD([[makeQuery(id+"F2.imprint","IMPRINT",EDGE,{"derivedFrom":subQ0}),-1.0]])]});}
            var Q11;
            {var subQ0=sQuery(id+"F2.wireOp",EDGE,"6fafc8a2-5585-4b41-b53a-40911dd4761f.2.0");Q11=makeQuery(id+"F2.imprint","IMPRINT",FACE,{"disambiguationData":[TD([[makeQuery(id+"F2.imprint","IMPRINT",EDGE,{"derivedFrom":subQ0}),-1.0]])]});}
            var Q12;
            {var subQ0=sQuery(id+"F2.wireOp",EDGE,"6fafc8a2-5585-4b41-b53a-40911dd4761f.1.0");Q12=makeQuery(id+"F2.imprint","IMPRINT",FACE,{"disambiguationData":[TD([[makeQuery(id+"F2.imprint","IMPRINT",EDGE,{"derivedFrom":subQ0}),-1.0]])]});}
            var Q13;
            {var subQ0=sQuery(id+"F2.wireOp",EDGE,"6fafc8a2-5585-4b41-b53a-40911dd4761f.7.0");Q13=makeQuery(id+"F2.imprint","IMPRINT",FACE,{"disambiguationData":[TD([[makeQuery(id+"F2.imprint","IMPRINT",EDGE,{"derivedFrom":subQ0}),-1.0]])]});}
            var Q14;
            {var subQ0=sQuery(id+"F2.wireOp",EDGE,"6fafc8a2-5585-4b41-b53a-40911dd4761f.6.0");Q14=makeQuery(id+"F2.imprint","IMPRINT",FACE,{"disambiguationData":[TD([[makeQuery(id+"F2.imprint","IMPRINT",EDGE,{"derivedFrom":subQ0}),-1.0]])]});}
            var Q15;
            {var subQ0=sQuery(id+"F2.wireOp",EDGE,"6fafc8a2-5585-4b41-b53a-40911dd4761f.5.0");Q15=makeQuery(id+"F2.imprint","IMPRINT",FACE,{"disambiguationData":[TD([[makeQuery(id+"F2.imprint","IMPRINT",EDGE,{"derivedFrom":subQ0}),-1.0]])]});}
            var Q16;
            {var subQ0=sQuery(id+"F2.wireOp",EDGE,"6fafc8a2-5585-4b41-b53a-40911dd4761f.4.0");Q16=makeQuery(id+"F2.imprint","IMPRINT",FACE,{"disambiguationData":[TD([[makeQuery(id+"F2.imprint","IMPRINT",EDGE,{"derivedFrom":subQ0}),-1.0]])]});}
            var Q17;
            {var subQ0=sQuery(id+"F2.wireOp",EDGE,"6fafc8a2-5585-4b41-b53a-40911dd4761f.3.0");Q17=makeQuery(id+"F2.imprint","IMPRINT",FACE,{"disambiguationData":[TD([[makeQuery(id+"F2.imprint","IMPRINT",EDGE,{"derivedFrom":subQ0}),-1.0]])]});}
            extrude(context, id + "F3", {"entities" : qUnion([Q0, Q1, Q2, Q3, Q4, Q5, Q6, Q7, Q8, Q9, Q10, Q11, Q12, Q13, Q14, Q15, Q16, Q17]), "operationType" : NewBodyOperationType.ADD, "depth" : 3.8 * mm});
        }
        {
            var Q0;
            Q0=qCreatedBy(makeId("Top.planeOp"),FACE);
            var sketch = newSketch(context, id + "F4", { "sketchPlane" : qUnion([Q0])});
            skCircle(sketch, "E4", {"center": v(0, -3.56) * mm, "radius": 0.65 * mm});
            skSolve(sketch);
        }
        {
            var Q0;
            Q0=makeQuery(id+"F4.imprint","IMPRINT",FACE,{"disambiguationData":[TD([[makeQuery(id+"F4.imprint","IMPRINT",EDGE,{"derivedFrom":sQuery(id+"F4.wireOp",EDGE,"E4")}),1.0]])]});
            extrude(context, id + "F5", {"entities" : qUnion([Q0]), "operationType" : NewBodyOperationType.REMOVE, "endBound" : BoundingType.UP_TO_NEXT, "depth" : 25 * mm});
        }
    });
